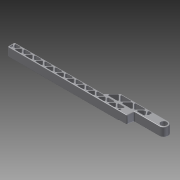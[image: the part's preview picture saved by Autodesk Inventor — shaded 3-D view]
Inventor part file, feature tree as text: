
AUTODESK INVENTOR PART (.ipt)
format: ipt  version: 2011 SP2 (Build 150309200, 309)  size: 971,264 bytes
history: native  units: mm
features: fillet x13, extrude x9, projected_geometry x8, sketch x7, plane x1, mirror x1
ambient origin geometry x8: Origin, YZ Plane, XZ Plane, XY Plane, X Axis, Y Axis, Z Axis, Center Point
feature tree (39):
  sketch  "Sketch1"  dims[d14=1.0mm d16=1.0mm]
  extrude  "Extrusion11"  Depth=1.0mm
  extrude  "Extrusion12"  Depth=1.0mm
  extrude  "Extrusion13"  Depth=16.580628mm
  extrude  "Extrusion14"  Depth=0.5mm
  extrude  "Extrusion15"  Depth=0.5mm
  extrude  "Extrusion16"  Depth=0.5mm
  fillet  "Fillet13"  Radius=0.5mm
  fillet  "Fillet14"  Radius=0.5mm
  fillet  "Fillet15"  Radius=0.5mm
  fillet  "Fillet16"  Radius=0.5mm
  fillet  "Fillet17"  Radius=0.5mm
  fillet  "Fillet18"  Radius=0.5mm
  fillet  "Fillet19"  Radius=0.5mm
  fillet  "Fillet20"  Radius=0.5mm
  fillet  "Fillet21"  Radius=0.5mm
  fillet  "Fillet22"  Radius=0.5mm
  fillet  "Fillet25"  Radius=0.5mm
  extrude  "Extrusion17"  Depth=0.5mm
  fillet  "Fillet26"  Radius=0.5mm
  extrude  "Extrusion18"  Depth=0.5mm
  fillet  "Fillet27"  Radius=0.5mm
  plane  "Work Plane2"
  mirror  "Mirror2"
  extrude  "Extrusion19"  Depth=0.5mm
  sketch  "Sketch11"  dims[d23=1.0mm d24=1.0mm]
  projected_geometry  "Projected Loop7"
  sketch  "Sketch12"  dims[d25=1.0mm d30=16.580628mm]
  projected_geometry  "Projected Loop8"
  projected_geometry  "Projected Loop9"
  sketch  "Sketch13"  dims[d32=1.0mm d62=0.5mm]
  sketch  "Sketch14"  dims[d64=0.5mm d65=0.5mm]
  sketch  "Sketch15"  dims[d66=0.5mm d68=0.5mm d69=0.5mm d70=0.5mm d71=0.5mm d72=0.5mm d73=0.5mm d74=0.5mm d75=0.5mm d76=0.5mm d77=0.5mm d78=0.5mm d79=0.5mm]
  projected_geometry  "Projected Loop10"
  projected_geometry  "Projected Loop11"
  projected_geometry  "Projected Loop12"
  projected_geometry  "Projected Loop13"
  projected_geometry  "Projected Loop14"
  sketch  "Sketch16"  dims[d80=0.5mm d81=0.5mm d82=0.5mm d83=0.5mm d84=0.5mm d85=0.5mm d86=0.5mm d87=0.5mm d88=0.5mm d89=0.5mm d90=0.5mm d91=0.5mm d92=0.5mm d93=0.5mm d94=0.5mm d95=0.5mm d96=0.5mm d97=0.5mm d98=0.5mm d99=0.5mm d100=0.5mm d101=0.5mm d102=0.5mm d103=0.5mm d104=0.5mm d106=0.5mm d107=0.5mm d108=0.5mm d109=0.5mm d115=14.209mm d116=3.912mm d120=5.45mm d121=3.75mm d122=1.875mm d124=2.725mm d126=3.060539mm d166=1.0mm d167=0.5mm d169=0.5mm d171=0.5mm d172=0.5mm d173=0.5mm d174=0.5mm d175=0.5mm d176=0.5mm d177=0.5mm d178=0.5mm d179=0.5mm d180=0.5mm d181=0.5mm d182=0.5mm d183=13.0mm d184=5.0mm d185=10.0mm d186=3.45mm d187=1.956mm d188=28.816511mm d189=34.516421mm d190=9.0mm d191=1.0mm d192=172.0mm d193=35.152794mm d194=10.0mm d195=0.0mm d196=10.0mm d197=0.0mm d198=6.85mm d199=0.0mm d200=10.0mm d201=8.0mm d202=0.0mm d203=14.835299mm d204=10.0mm d205=0.0mm d206=16.580628mm d207=10.0mm d208=0.0mm d209=1.0mm d210=1.0mm d211=0.5mm d212=1.75mm d213=0.2mm d214=1.0mm d215=0.5mm d216=0.5mm d217=0.5mm d218=1.0mm d221=2.25mm d222=10.0mm d223=0.0mm d224=0.75mm d225=10.0mm d226=0.0mm d227=0.5mm d228=-175.0mm d229=1.0mm d230=11.0mm d231=0.0mm d232=0.0mm]
